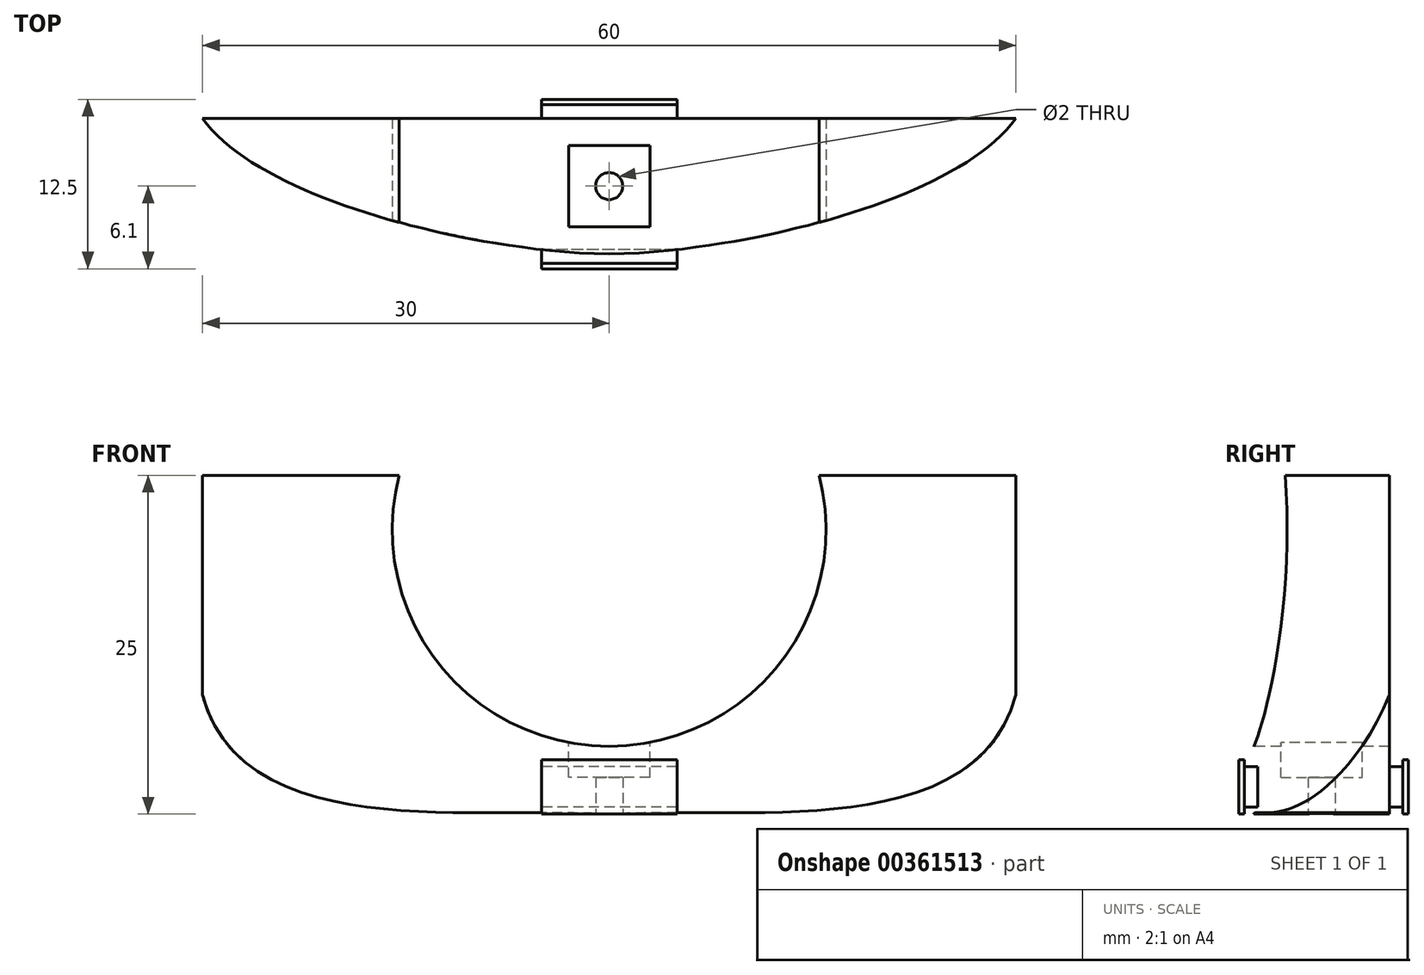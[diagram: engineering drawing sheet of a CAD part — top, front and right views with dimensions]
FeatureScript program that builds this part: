
annotation { "Feature Type Name" : "Feature", "Feature Type Description" : "" }
export const myFeature = defineFeature(function(context is Context, id is Id, definition is map)
    precondition{}
    {
        {
            var Q0;
            Q0=qCreatedBy(makeId("Top.planeOp"),FACE);
            var sketch = newSketch(context, id + "F0", { "sketchPlane" : qUnion([Q0])});
            skLineSegment(sketch, "E0", {"start": v(0, 0) * mm, "end": v(30, 0) * mm});
            skFitSpline(sketch, "E1.MirrorCS", {"points": [v(0, -10) * mm, v(30, 0) * mm], "startDerivative": vector(26.01, 0.07) * mm, "endDerivative": vector(13.6, 19.1) * mm});
            skFitSpline(sketch, "E2.MirrorCS", {"points": [v(0, -10) * mm, v(-30, 0) * mm], "startDerivative": vector(-26.01, 0.07) * mm, "endDerivative": vector(-13.6, 19.1) * mm});
            skLineSegment(sketch, "E3.MirrorCS", {"start": v(0, 0) * mm, "end": v(-30, 0) * mm});
            skLineSegment(sketch, "E4", {"start": v(0, -10) * mm, "end": v(0, 0) * mm});
            skLineSegment(sketch, "E5", {"start": v(0, 0) * mm, "end": v(0, -5) * mm});
            skCircle(sketch, "E6", {"center": v(0, -5) * mm, "radius": 1 * mm});
            skSolve(sketch);
        }
        {
            var Q0;
            {var subQ0=sQuery(id+"F0.wireOp",EDGE,"E1.MirrorCS");Q0=makeQuery(id+"F0.imprint","IMPRINT",FACE,{"disambiguationData":[TD([[makeQuery(id+"F0.imprint","IMPRINT",EDGE,{"derivedFrom":subQ0}),1.0]])]});}
            var Q1;
            {var subQ0=sQuery(id+"F0.wireOp",EDGE,"E2.MirrorCS");Q1=makeQuery(id+"F0.imprint","IMPRINT",FACE,{"disambiguationData":[TD([[makeQuery(id+"F0.imprint","IMPRINT",EDGE,{"derivedFrom":subQ0}),-1.0]])]});}
            extrude(context, id + "F1", {"entities" : qUnion([Q0, Q1]), "depth" : 25 * mm});
        }
        {
            var Q0;
            Q0=qCreatedBy(makeId("Front.planeOp"),FACE);
            var sketch = newSketch(context, id + "F2", { "sketchPlane" : qUnion([Q0])});
            skLineSegment(sketch, "E7", {"start": v(0, 0) * mm, "end": v(0, 21) * mm});
            skCircle(sketch, "E8", {"center": v(0, 21) * mm, "radius": 16 * mm});
            skLineSegment(sketch, "E9.bottom", {"start": v(5, 3.5) * mm, "end": v(-5, 3.5) * mm});
            skLineSegment(sketch, "E9.top", {"start": v(5, 0.5) * mm, "end": v(-5, 0.5) * mm});
            skLineSegment(sketch, "E9.left", {"start": v(5, 3.5) * mm, "end": v(5, 0.5) * mm});
            skLineSegment(sketch, "E9.right", {"start": v(-5, 3.5) * mm, "end": v(-5, 0.5) * mm});
            skPoint(sketch, "E9.middle", {"position": v(0, 2) * mm});
            skLineSegment(sketch, "E10.bottom", {"start": v(-5, 0) * mm, "end": v(5, 0) * mm});
            skLineSegment(sketch, "E10.top", {"start": v(-5, 4) * mm, "end": v(5, 4) * mm});
            skLineSegment(sketch, "E10.left", {"start": v(-5, 0) * mm, "end": v(-5, 4) * mm});
            skLineSegment(sketch, "E10.right", {"start": v(5, 0) * mm, "end": v(5, 4) * mm});
            skSolve(sketch);
        }
        {
            var Q0;
            Q0=makeQuery(id+"F2.imprint","IMPRINT",FACE,{"disambiguationData":[TD([[makeQuery(id+"F2.imprint","IMPRINT",EDGE,{"derivedFrom":sQuery(id+"F2.wireOp",EDGE,"E8")}),1.0]])]});
            extrude(context, id + "F3", {"entities" : qUnion([Q0]), "operationType" : NewBodyOperationType.REMOVE, "endBound" : BoundingType.SYMMETRIC, "oppositeDirection" : true, "depth" : 25 * mm});
        }
        {
            var Q0;
            Q0=qCreatedBy(makeId("Top.planeOp"),FACE);
            var sketch = newSketch(context, id + "F4", { "sketchPlane" : qUnion([Q0])});
            skLineSegment(sketch, "E11.bottom", {"start": v(3, -8) * mm, "end": v(-3, -8) * mm});
            skLineSegment(sketch, "E11.top", {"start": v(3, -2) * mm, "end": v(-3, -2) * mm});
            skLineSegment(sketch, "E11.left", {"start": v(3, -8) * mm, "end": v(3, -2) * mm});
            skLineSegment(sketch, "E11.right", {"start": v(-3, -8) * mm, "end": v(-3, -2) * mm});
            skPoint(sketch, "E11.middle", {"position": v(0, -5) * mm});
            skLineSegment(sketch, "E12", {"start": v(0, -5) * mm, "end": v(0, 0) * mm});
            skSolve(sketch);
        }
        {
            var Q0;
            Q0=makeQuery(id+"F4.imprint","IMPRINT",FACE,{"disambiguationData":[TD([[makeQuery(id+"F4.imprint","IMPRINT",EDGE,{"derivedFrom":sQuery(id+"F4.wireOp",EDGE,"E11.bottom")}),-1.0]])]});
            extrude(context, id + "F5", {"entities" : qUnion([Q0]), "oppositeDirection" : true, "depth" : 3 * mm});
        }
        {
            var Q0;
            Q0=makeQuery(id+"F5.opExtrude","SWEPT_BODY",BODY,{"disambiguationData":[OSD([sQuery(id+"F4.wireOp",EDGE,"E11.bottom"),sQuery(id+"F4.wireOp",EDGE,"E11.top"),sQuery(id+"F4.wireOp",EDGE,"E11.left"),sQuery(id+"F4.wireOp",EDGE,"E11.right")])]});
            transform(context, id + "F6", {"entities" : qUnion([Q0]), "transformType" : TransformType.TRANSLATION_3D, "dx" : 0 * mm, "dy" : 0 * mm, "dz" : 5.7 * mm, "makeCopy" : false});
        }
        {
            var Q0;
            Q0=makeQuery(id+"F5.opExtrude","SWEPT_BODY",BODY,{"disambiguationData":[OSD([sQuery(id+"F4.wireOp",EDGE,"E11.bottom"),sQuery(id+"F4.wireOp",EDGE,"E11.top"),sQuery(id+"F4.wireOp",EDGE,"E11.left"),sQuery(id+"F4.wireOp",EDGE,"E11.right")])]});
            var Q1;
            Q1=makeQuery(id+"F1.opExtrude","SWEPT_BODY",BODY,{"disambiguationData":[OSD([sQuery(id+"F0.wireOp",EDGE,"e03d7212-f5a5-47f4-b16b-fabad3bf94a4"),sQuery(id+"F0.wireOp",EDGE,"E1.MirrorCS"),sQuery(id+"F0.wireOp",EDGE,"E2.MirrorCS"),sQuery(id+"F0.wireOp",EDGE,"407b53cb-9c28-4881-a71b-1919ee9b0bba0.MirrorCS"),sQuery(id+"F0.wireOp",EDGE,"tGvWhP2G-i5Zm-Vjij-1rL3-US4fvbQdiM4k")])]});
            booleanBodies(context, id + "F7", {"operationType" : BooleanOperationType.SUBTRACTION, "tools" : qUnion([Q0]), "targets" : qUnion([Q1])});
        }
        {
            var Q0;
            Q0=qCreatedBy(makeId("Front.planeOp"),FACE);
            var sketch = newSketch(context, id + "F8", { "sketchPlane" : qUnion([Q0])});
            skFitSpline(sketch, "E13", {"points": [v(0, 0) * mm, v(-30.1, 9.24) * mm], "startDerivative": vector(-31.49, 1.82) * mm, "endDerivative": vector(-7.79, 34.36) * mm});
            skLineSegment(sketch, "E14", {"start": v(-30.1, 9.24) * mm, "end": v(-30.1, -0.6) * mm});
            skLineSegment(sketch, "E15", {"start": v(-30.1, -0.6) * mm, "end": v(0, -0.6) * mm});
            skFitSpline(sketch, "E16.MirrorCS", {"points": [v(0, 0) * mm, v(30.1, 9.24) * mm], "startDerivative": vector(31.49, 1.82) * mm, "endDerivative": vector(7.79, 34.36) * mm});
            skLineSegment(sketch, "E17.MirrorCS", {"start": v(30.1, 9.24) * mm, "end": v(30.1, -0.6) * mm});
            skLineSegment(sketch, "E18.MirrorCS", {"start": v(30.1, -0.6) * mm, "end": v(0, -0.6) * mm});
            skSolve(sketch);
        }
        {
            var Q0;
            Q0=makeQuery(id+"F8.imprint","IMPRINT",FACE,{"disambiguationData":[TD([[makeQuery(id+"F8.imprint","IMPRINT",EDGE,{"derivedFrom":sQuery(id+"F8.wireOp",EDGE,"E13")}),1.0]])]});
            extrude(context, id + "F9", {"entities" : qUnion([Q0]), "operationType" : NewBodyOperationType.REMOVE, "endBound" : BoundingType.SYMMETRIC, "oppositeDirection" : true, "depth" : 25 * mm});
        }
        {
            var Q0;
            {var subQ0=sQuery(id+"F2.wireOp",EDGE,"E10.bottom");var subQ1=sQuery(id+"F2.wireOp",EDGE,"E7");var subQ2=makeQuery(id+"F2.imprint","INTERSECT",VERTEX,{"derivedFrom":[subQ1,subQ0]});Q0=makeQuery(id+"F2.imprint","IMPRINT",FACE,{"disambiguationData":[TD([[makeQuery(id+"F2.imprint","IMPRINT",EDGE,{"disambiguationData":[TD([[subQ2,-1.0]])],"derivedFrom":subQ1}),-1.0]])]});}
            var Q1;
            {var subQ0=sQuery(id+"F2.wireOp",EDGE,"E10.bottom");var subQ1=sQuery(id+"F2.wireOp",EDGE,"E7");var subQ2=makeQuery(id+"F2.imprint","INTERSECT",VERTEX,{"derivedFrom":[subQ1,subQ0]});Q1=makeQuery(id+"F2.imprint","IMPRINT",FACE,{"disambiguationData":[TD([[makeQuery(id+"F2.imprint","IMPRINT",EDGE,{"disambiguationData":[TD([[subQ2,-1.0]])],"derivedFrom":subQ1}),1.0]])]});}
            var Q2;
            {var subQ0=sQuery(id+"F2.wireOp",EDGE,"E9.top");var subQ1=sQuery(id+"F2.wireOp",EDGE,"E7");var subQ2=makeQuery(id+"F2.imprint","INTERSECT",VERTEX,{"derivedFrom":[subQ1,subQ0]});Q2=makeQuery(id+"F2.imprint","IMPRINT",FACE,{"disambiguationData":[TD([[makeQuery(id+"F2.imprint","IMPRINT",EDGE,{"disambiguationData":[TD([[subQ2,-1.0]])],"derivedFrom":subQ1}),1.0]])]});}
            var Q3;
            {var subQ0=sQuery(id+"F2.wireOp",EDGE,"E9.top");var subQ1=sQuery(id+"F2.wireOp",EDGE,"E7");var subQ2=makeQuery(id+"F2.imprint","INTERSECT",VERTEX,{"derivedFrom":[subQ1,subQ0]});Q3=makeQuery(id+"F2.imprint","IMPRINT",FACE,{"disambiguationData":[TD([[makeQuery(id+"F2.imprint","IMPRINT",EDGE,{"disambiguationData":[TD([[subQ2,-1.0]])],"derivedFrom":subQ1}),-1.0]])]});}
            var Q4;
            {var subQ0=sQuery(id+"F2.wireOp",EDGE,"E10.top");var subQ1=sQuery(id+"F2.wireOp",EDGE,"E7");var subQ2=makeQuery(id+"F2.imprint","INTERSECT",VERTEX,{"derivedFrom":[subQ1,subQ0]});Q4=makeQuery(id+"F2.imprint","IMPRINT",FACE,{"disambiguationData":[TD([[makeQuery(id+"F2.imprint","IMPRINT",EDGE,{"disambiguationData":[TD([[subQ2,1.0]])],"derivedFrom":subQ1}),-1.0]])]});}
            var Q5;
            {var subQ0=sQuery(id+"F2.wireOp",EDGE,"E10.top");var subQ1=sQuery(id+"F2.wireOp",EDGE,"E7");var subQ2=makeQuery(id+"F2.imprint","INTERSECT",VERTEX,{"derivedFrom":[subQ1,subQ0]});Q5=makeQuery(id+"F2.imprint","IMPRINT",FACE,{"disambiguationData":[TD([[makeQuery(id+"F2.imprint","IMPRINT",EDGE,{"disambiguationData":[TD([[subQ2,1.0]])],"derivedFrom":subQ1}),1.0]])]});}
            extrude(context, id + "F10", {"entities" : qUnion([Q0, Q1, Q2, Q3, Q4, Q5]), "oppositeDirection" : true, "depth" : .4 * mm});
        }
        {
            var Q0;
            {var subQ0=sQuery(id+"F2.wireOp",EDGE,"E9.top");var subQ1=sQuery(id+"F2.wireOp",EDGE,"E7");var subQ2=makeQuery(id+"F2.imprint","INTERSECT",VERTEX,{"derivedFrom":[subQ1,subQ0]});Q0=makeQuery(id+"F2.imprint","IMPRINT",FACE,{"disambiguationData":[TD([[makeQuery(id+"F2.imprint","IMPRINT",EDGE,{"disambiguationData":[TD([[subQ2,-1.0]])],"derivedFrom":subQ1}),1.0]])]});}
            var Q1;
            {var subQ0=sQuery(id+"F2.wireOp",EDGE,"E9.top");var subQ1=sQuery(id+"F2.wireOp",EDGE,"E7");var subQ2=makeQuery(id+"F2.imprint","INTERSECT",VERTEX,{"derivedFrom":[subQ1,subQ0]});Q1=makeQuery(id+"F2.imprint","IMPRINT",FACE,{"disambiguationData":[TD([[makeQuery(id+"F2.imprint","IMPRINT",EDGE,{"disambiguationData":[TD([[subQ2,-1.0]])],"derivedFrom":subQ1}),-1.0]])]});}
            extrude(context, id + "F11", {"entities" : qUnion([Q0, Q1]), "oppositeDirection" : true, "depth" : 1 * mm});
        }
        {
            var Q0;
            Q0=makeQuery(id+"F11.opExtrude","SWEPT_BODY",BODY,{"disambiguationData":[OSD([sQuery(id+"F2.wireOp",EDGE,"E9.bottom"),sQuery(id+"F2.wireOp",EDGE,"E9.top"),sQuery(id+"F2.wireOp",EDGE,"E10.left"),sQuery(id+"F2.wireOp",EDGE,"E10.right")])]});
            transform(context, id + "F12", {"entities" : qUnion([Q0]), "transformType" : TransformType.TRANSLATION_3D, "dx" : 0 * mm, "dy" : -10.7 * mm, "dz" : 0 * mm, "makeCopy" : true});
        }
        {
            var Q0;
            Q0=makeQuery(id+"F10.opExtrude","SWEPT_BODY",BODY,{"disambiguationData":[OSD([sQuery(id+"F2.wireOp",EDGE,"E10.bottom"),sQuery(id+"F2.wireOp",EDGE,"E10.top"),sQuery(id+"F2.wireOp",EDGE,"E10.left"),sQuery(id+"F2.wireOp",EDGE,"E10.right")])]});
            transform(context, id + "F13", {"entities" : qUnion([Q0]), "transformType" : TransformType.TRANSLATION_3D, "dx" : 0 * mm, "dy" : 1 * mm, "dz" : 0 * mm, "makeCopy" : false});
        }
        {
            var Q0;
            Q0=makeQuery(id+"F10.opExtrude","SWEPT_BODY",BODY,{"disambiguationData":[OSD([sQuery(id+"F2.wireOp",EDGE,"E10.bottom"),sQuery(id+"F2.wireOp",EDGE,"E10.top"),sQuery(id+"F2.wireOp",EDGE,"E10.left"),sQuery(id+"F2.wireOp",EDGE,"E10.right")])]});
            transform(context, id + "F14", {"entities" : qUnion([Q0]), "transformType" : TransformType.TRANSLATION_3D, "dx" : 0 * mm, "dy" : -12.1 * mm, "dz" : 0 * mm, "makeCopy" : true});
        }
    });
